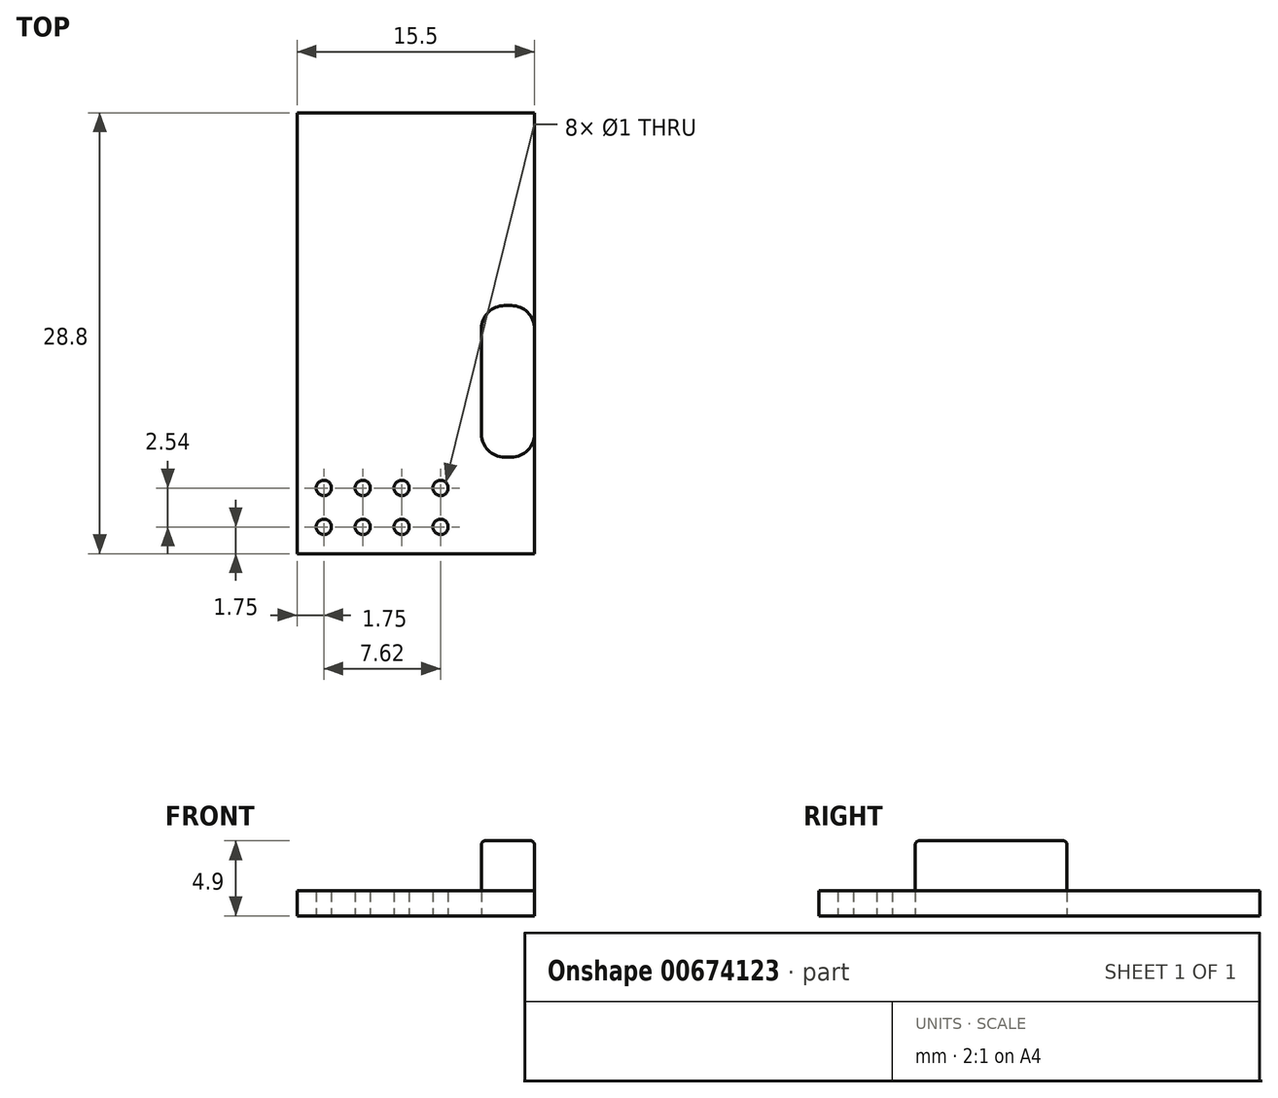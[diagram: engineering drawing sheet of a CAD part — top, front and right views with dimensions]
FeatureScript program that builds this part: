
annotation { "Feature Type Name" : "Feature", "Feature Type Description" : "" }
export const myFeature = defineFeature(function(context is Context, id is Id, definition is map)
    precondition{}
    {
        {
            var Q0;
            Q0=qCreatedBy(makeId("Top.planeOp"),FACE);
            var sketch = newSketch(context, id + "F0", { "sketchPlane" : qUnion([Q0])});
            skLineSegment(sketch, "E0.bottom", {"start": v(7.75, 14.4) * mm, "end": v(-7.75, 14.4) * mm});
            skLineSegment(sketch, "E0.top", {"start": v(7.75, -14.4) * mm, "end": v(-7.75, -14.4) * mm});
            skLineSegment(sketch, "E0.left", {"start": v(7.75, 14.4) * mm, "end": v(7.75, -14.4) * mm});
            skLineSegment(sketch, "E0.right", {"start": v(-7.75, 14.4) * mm, "end": v(-7.75, -14.4) * mm});
            skPoint(sketch, "E0.middle", {"position": v(0, 0) * mm});
            skLineSegment(sketch, "E1.bottom", {"start": v(6.25, 1.8) * mm, "end": v(5.8, 1.8) * mm});
            skLineSegment(sketch, "E1.top", {"start": v(6.25, -8.1) * mm, "end": v(5.8, -8.1) * mm});
            skLineSegment(sketch, "E1.left", {"start": v(7.75, 0.3) * mm, "end": v(7.75, -6.6) * mm});
            skLineSegment(sketch, "E1.right", {"start": v(4.3, 0.3) * mm, "end": v(4.3, -6.6) * mm});
            skPoint(sketch, "E2.visualSharp", {"position": v(4.3, 1.8) * mm});
            skArc(sketch, "E2.filletArc", {"start": v(5.8, 1.8) * mm, "mid": v(4.74, 1.36) * mm, "end": v(4.3, 0.3) * mm});
            skPoint(sketch, "E3.visualSharp", {"position": v(7.75, 1.8) * mm});
            skArc(sketch, "E3.filletArc", {"start": v(7.75, 0.3) * mm, "mid": v(7.31, 1.36) * mm, "end": v(6.25, 1.8) * mm});
            skPoint(sketch, "E4.visualSharp", {"position": v(4.3, -8.1) * mm});
            skArc(sketch, "E4.filletArc", {"start": v(4.3, -6.6) * mm, "mid": v(4.74, -7.66) * mm, "end": v(5.8, -8.1) * mm});
            skPoint(sketch, "E5.visualSharp", {"position": v(7.75, -8.1) * mm});
            skArc(sketch, "E5.filletArc", {"start": v(6.25, -8.1) * mm, "mid": v(7.31, -7.66) * mm, "end": v(7.75, -6.6) * mm});
            skCircle(sketch, "E6", {"center": v(-6, -12.65) * mm, "radius": 0.5 * mm});
            skCircle(sketch, "E7.0.1.0", {"center": v(-6, -10.11) * mm, "radius": 0.5 * mm});
            skCircle(sketch, "E7.1.0.0", {"center": v(-3.46, -12.65) * mm, "radius": 0.5 * mm});
            skCircle(sketch, "E7.1.1.0", {"center": v(-3.46, -10.11) * mm, "radius": 0.5 * mm});
            skCircle(sketch, "E7.2.0.0", {"center": v(-0.92, -12.65) * mm, "radius": 0.5 * mm});
            skCircle(sketch, "E7.2.1.0", {"center": v(-0.92, -10.11) * mm, "radius": 0.5 * mm});
            skCircle(sketch, "E7.3.0.0", {"center": v(1.62, -12.65) * mm, "radius": 0.5 * mm});
            skCircle(sketch, "E7.3.1.0", {"center": v(1.62, -10.11) * mm, "radius": 0.5 * mm});
            skLineSegment(sketch, "E7.direction1", {"start": v(-6, -12.65) * mm, "end": v(-3.46, -12.65) * mm, "construction": true});
            skLineSegment(sketch, "E7.direction2", {"start": v(-6, -12.65) * mm, "end": v(-6, -10.11) * mm, "construction": true});
            skSolve(sketch);
        }
        {
            var Q0;
            {var subQ1=sQuery(id+"F0.wireOp",EDGE,"E0.bottom");Q0=makeQuery(id+"F0.imprint","IMPRINT",FACE,{"disambiguationData":[TD([[makeQuery(id+"F0.imprint","IMPRINT",EDGE,{"derivedFrom":subQ1}),1.0]])]});}
            var Q1;
            Q1=makeQuery(id+"F0.imprint","IMPRINT",FACE,{"disambiguationData":[TD([[makeQuery(id+"F0.imprint","IMPRINT",EDGE,{"derivedFrom":sQuery(id+"F0.wireOp",EDGE,"E1.bottom")}),1.0]])]});
            extrude(context, id + "F1", {"entities" : qUnion([Q0, Q1]), "depth" : 1.65 * mm, "offsetDistance" : 25 * mm});
        }
        {
            var Q0;
            Q0=makeQuery(id+"F0.imprint","IMPRINT",FACE,{"disambiguationData":[TD([[makeQuery(id+"F0.imprint","IMPRINT",EDGE,{"derivedFrom":sQuery(id+"F0.wireOp",EDGE,"E1.bottom")}),1.0]])]});
            extrude(context, id + "F2", {"entities" : qUnion([Q0]), "depth" : 4.9 * mm, "offsetDistance" : 25 * mm});
        }
        {
            var Q0;
            Q0=makeQuery(id+"F2.opExtrude","CAP_FACE",FACE,{"disambiguationData":[OSD([sQuery(id+"F0.wireOp",EDGE,"E1.bottom"),sQuery(id+"F0.wireOp",EDGE,"E1.top"),sQuery(id+"F0.wireOp",EDGE,"E1.left"),sQuery(id+"F0.wireOp",EDGE,"E1.right"),sQuery(id+"F0.wireOp",EDGE,"E2.filletArc"),sQuery(id+"F0.wireOp",EDGE,"E3.filletArc"),sQuery(id+"F0.wireOp",EDGE,"E4.filletArc"),sQuery(id+"F0.wireOp",EDGE,"E5.filletArc")])],"isStart":false});
            fillet(context, id + "F3", {"entities" : qUnion([Q0]), "radius" : .25 * mm, "tangentPropagation" : true, "allowEdgeOverflow" : false});
        }
    });
